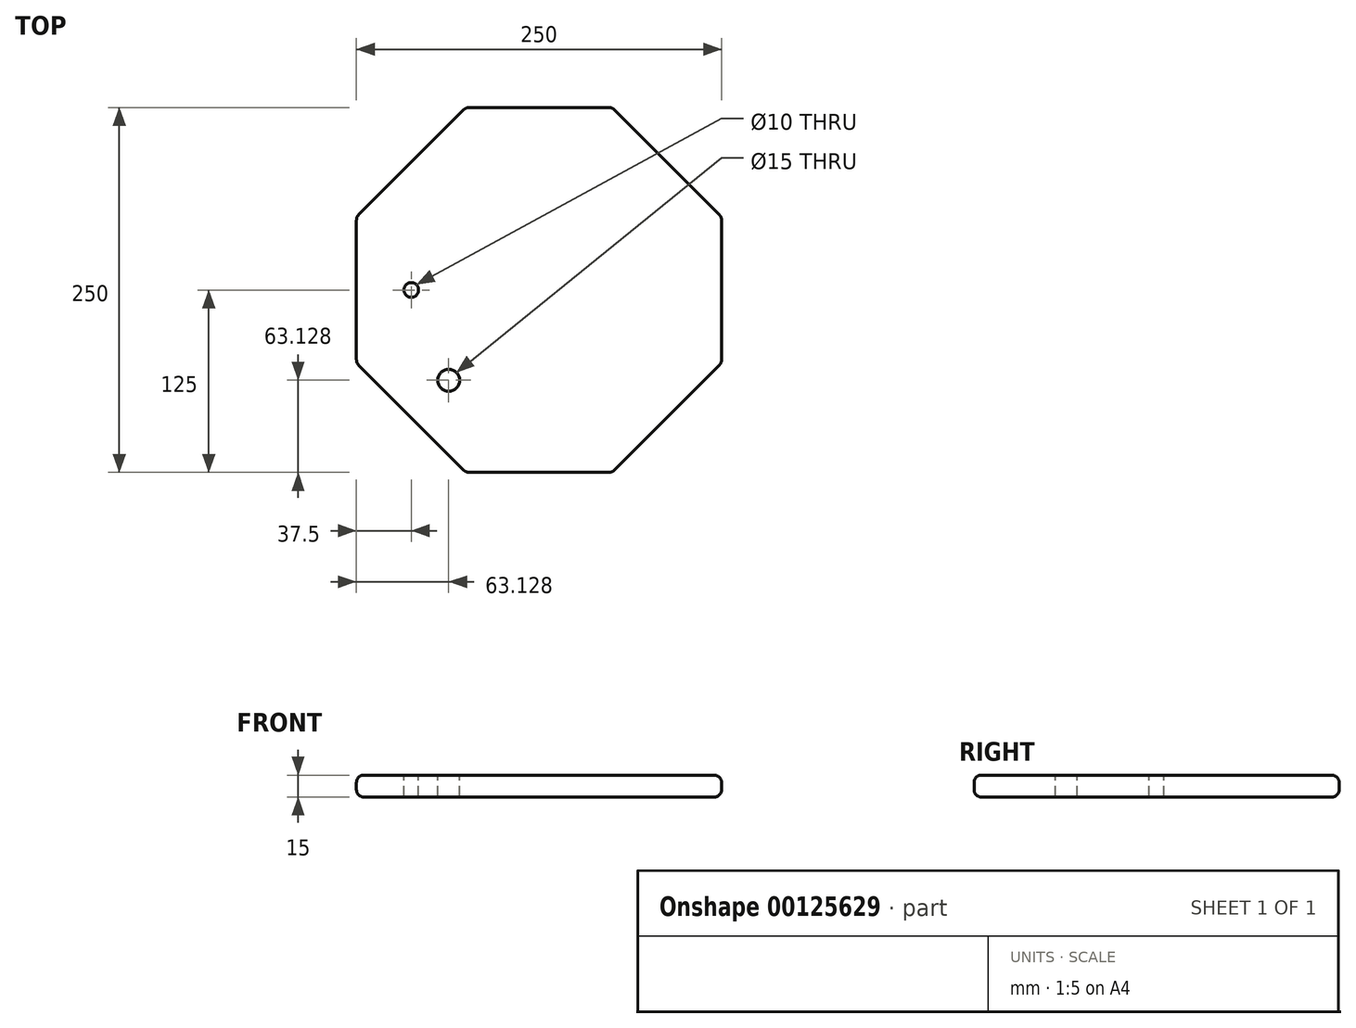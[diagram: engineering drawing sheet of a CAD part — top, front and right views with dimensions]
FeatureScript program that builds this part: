
annotation { "Feature Type Name" : "Feature", "Feature Type Description" : "" }
export const myFeature = defineFeature(function(context is Context, id is Id, definition is map)
    precondition{}
    {
        {
            var Q0;
            Q0=qCreatedBy(makeId("Top.planeOp"),FACE);
            var sketch = newSketch(context, id + "F0", { "sketchPlane" : qUnion([Q0])});
            skLineSegment(sketch, "E0.bottom", {"start": v(-125, 125) * mm, "end": v(125, 125) * mm});
            skLineSegment(sketch, "E0.top", {"start": v(-125, -125) * mm, "end": v(125, -125) * mm});
            skLineSegment(sketch, "E0.left", {"start": v(-125, 125) * mm, "end": v(-125, -125) * mm});
            skLineSegment(sketch, "E0.right", {"start": v(125, 125) * mm, "end": v(125, -125) * mm});
            skSolve(sketch);
        }
        {
            var Q0;
            Q0 = qSketchRegion(id + "F0", true);
            extrude(context, id + "F1", {"entities" : qUnion([Q0]), "depth" : 15 * mm});
        }
        {
            var Q0;
            Q0=qCreatedBy(makeId("Front.planeOp"),FACE);
            var sketch = newSketch(context, id + "F2", { "sketchPlane" : qUnion([Q0])});
            skLineSegment(sketch, "E1", {"start": v(0, 43.74) * mm, "end": v(0, -57.22) * mm, "construction": true});
            skSolve(sketch);
        }
        {
            var Q0;
            Q0=makeQuery(id+"F1.opExtrude","CAP_FACE",FACE,{"disambiguationData":[OSD([sQuery(id+"F0.wireOp",EDGE,"E0.bottom"),sQuery(id+"F0.wireOp",EDGE,"E0.top"),sQuery(id+"F0.wireOp",EDGE,"E0.left"),sQuery(id+"F0.wireOp",EDGE,"E0.right")])],"isStart":false});
            var sketch = newSketch(context, id + "F3", { "sketchPlane" : qUnion([Q0])});
            skCircle(sketch, "E2", {"center": v(-87.5, 0) * mm, "radius": 5 * mm});
            skSolve(sketch);
        }
        {
            var Q0;
            Q0 = qSketchRegion(id + "F3", true);
            extrude(context, id + "F4", {"entities" : qUnion([Q0]), "operationType" : NewBodyOperationType.REMOVE, "endBound" : BoundingType.THROUGH_ALL, "oppositeDirection" : true, "depth" : 25 * mm});
        }
        {
            var Q0;
            Q0=qCreatedBy(makeId("Front.planeOp"),FACE);
            var Q1;
            Q1=qCreatedBy(makeId("Right.planeOp"),FACE);
            cPlane(context, id + "F5", {"entities" : qUnion([Q0, Q1]), "cplaneType" : CPlaneType.MID_PLANE, "offset" : 25 * mm, "flipAlignment" : true, "width" : 150 * mm, "height" : 150 * mm});
        }
        {
            var Q0;
            Q0=makeQuery(id+"F1.opExtrude","CAP_FACE",FACE,{"disambiguationData":[OSD([sQuery(id+"F0.wireOp",EDGE,"E0.bottom"),sQuery(id+"F0.wireOp",EDGE,"E0.top"),sQuery(id+"F0.wireOp",EDGE,"E0.left"),sQuery(id+"F0.wireOp",EDGE,"E0.right")])],"isStart":false});
            var sketch = newSketch(context, id + "F6", { "sketchPlane" : qUnion([Q0])});
            skCircle(sketch, "E3", {"center": v(-61.87, -61.87) * mm, "radius": 7.5 * mm});
            skSolve(sketch);
        }
        {
            var Q0;
            Q0=makeQuery(id+"F6.imprint","IMPRINT",FACE,{"disambiguationData":[TD([[makeQuery(id+"F6.imprint","IMPRINT",EDGE,{"derivedFrom":sQuery(id+"F6.wireOp",EDGE,"E3")}),1.0]])]});
            extrude(context, id + "F7", {"entities" : qUnion([Q0]), "operationType" : NewBodyOperationType.REMOVE, "endBound" : BoundingType.THROUGH_ALL, "oppositeDirection" : true, "depth" : 25 * mm});
        }
        {
            var Q0;
            Q0=makeQuery(id+"F1.opExtrude","SWEPT_EDGE",EDGE,{"disambiguationData":[OSD([sQuery(id+"F0.wireOp",EDGE,"E0.bottom"),sQuery(id+"F0.wireOp",EDGE,"E0.left")])]});
            var Q1;
            Q1=makeQuery(id+"F1.opExtrude","SWEPT_EDGE",EDGE,{"disambiguationData":[OSD([sQuery(id+"F0.wireOp",EDGE,"E0.top"),sQuery(id+"F0.wireOp",EDGE,"E0.left")])]});
            var Q2;
            Q2=makeQuery(id+"F1.opExtrude","SWEPT_EDGE",EDGE,{"disambiguationData":[OSD([sQuery(id+"F0.wireOp",EDGE,"E0.top"),sQuery(id+"F0.wireOp",EDGE,"E0.right")])]});
            var Q3;
            Q3=makeQuery(id+"F1.opExtrude","SWEPT_EDGE",EDGE,{"disambiguationData":[OSD([sQuery(id+"F0.wireOp",EDGE,"E0.bottom"),sQuery(id+"F0.wireOp",EDGE,"E0.right")])]});
            chamfer(context, id + "F8", {"entities" : qUnion([Q0, Q1, Q2, Q3]), "width" : 75 * mm, "tangentPropagation" : true});
        }
        {
            var Q0;
            Q0=makeQuery(id+"F1.opExtrude","CAP_EDGE",EDGE,{"disambiguationData":[OSD([sQuery(id+"F0.wireOp",EDGE,"E0.left")])],"isStart":false});
            var Q1;
            Q1=makeQuery(id+"F1.opExtrude","SWEPT_FACE",FACE,{"disambiguationData":[OSD([sQuery(id+"F0.wireOp",EDGE,"E0.left")])]});
            var Q2;
            Q2=makeQuery(id+"F8.opChamfer","BLEND_FACE",FACE,{"disambiguationData":[OSD([sQuery(id+"F0.wireOp",EDGE,"E0.top"),sQuery(id+"F0.wireOp",EDGE,"E0.left")])]});
            var Q3;
            Q3=makeQuery(id+"F1.opExtrude","SWEPT_FACE",FACE,{"disambiguationData":[OSD([sQuery(id+"F0.wireOp",EDGE,"E0.top")])]});
            var Q4;
            Q4=makeQuery(id+"F8.opChamfer","BLEND_FACE",FACE,{"disambiguationData":[OSD([sQuery(id+"F0.wireOp",EDGE,"E0.top"),sQuery(id+"F0.wireOp",EDGE,"E0.right")])]});
            var Q5;
            Q5=makeQuery(id+"F1.opExtrude","SWEPT_FACE",FACE,{"disambiguationData":[OSD([sQuery(id+"F0.wireOp",EDGE,"E0.right")])]});
            var Q6;
            Q6=makeQuery(id+"F8.opChamfer","BLEND_FACE",FACE,{"disambiguationData":[OSD([sQuery(id+"F0.wireOp",EDGE,"E0.bottom"),sQuery(id+"F0.wireOp",EDGE,"E0.right")])]});
            var Q7;
            Q7=makeQuery(id+"F1.opExtrude","SWEPT_FACE",FACE,{"disambiguationData":[OSD([sQuery(id+"F0.wireOp",EDGE,"E0.bottom")])]});
            var Q8;
            Q8=makeQuery(id+"F8.opChamfer","BLEND_FACE",FACE,{"disambiguationData":[OSD([sQuery(id+"F0.wireOp",EDGE,"E0.bottom"),sQuery(id+"F0.wireOp",EDGE,"E0.left")])]});
            fillet(context, id + "F9", {"entities" : qUnion([Q0, Q1, Q2, Q3, Q4, Q5, Q6, Q7, Q8]), "radius" : 5 * mm, "tangentPropagation" : true, "allowEdgeOverflow" : false});
        }
    });
